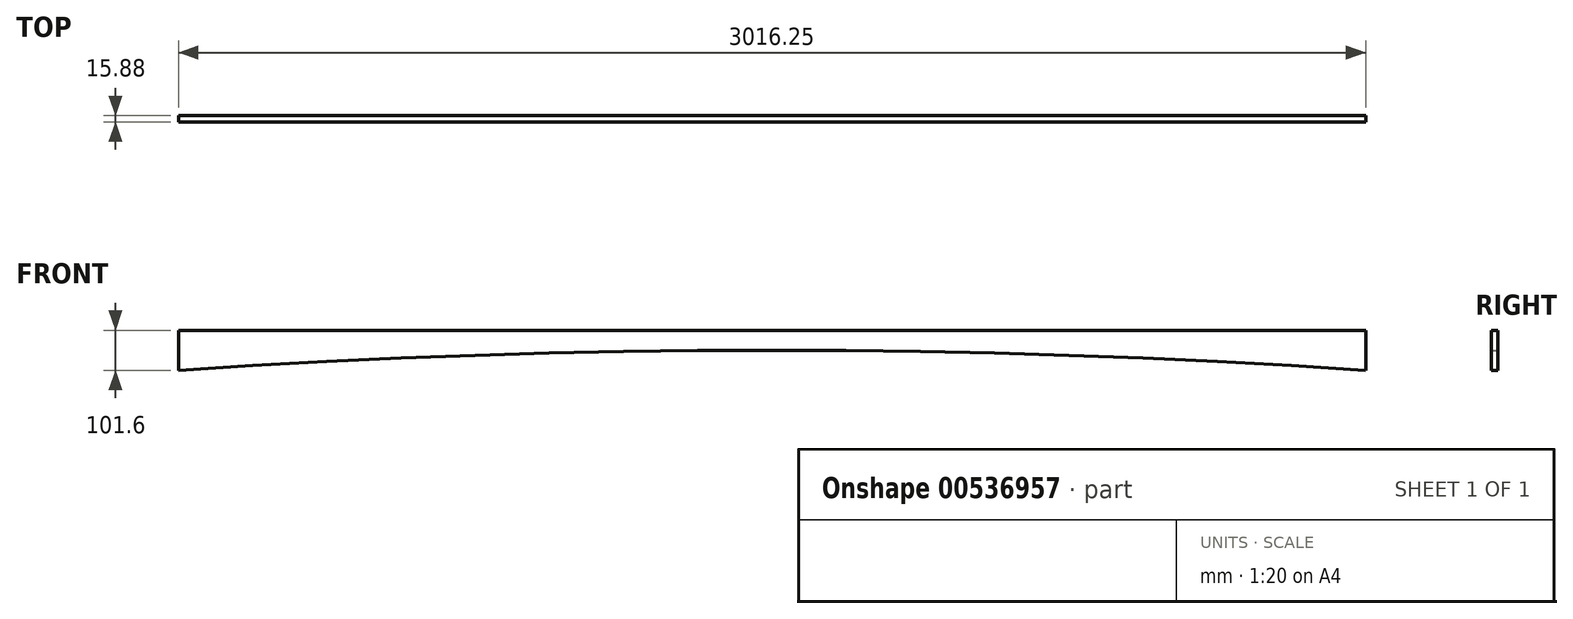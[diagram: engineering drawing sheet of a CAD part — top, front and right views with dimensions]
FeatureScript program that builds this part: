
annotation { "Feature Type Name" : "Feature", "Feature Type Description" : "" }
export const myFeature = defineFeature(function(context is Context, id is Id, definition is map)
    precondition{}
    {
        {
            var Q0;
            Q0=qCreatedBy(makeId("Front.planeOp"),FACE);
            var sketch = newSketch(context, id + "F0", { "sketchPlane" : qUnion([Q0])});
            skLineSegment(sketch, "E0", {"start": v(-115.17, 28.94) * mm, "end": v(3002.68, 28.94) * mm});
            skLineSegment(sketch, "E1", {"start": v(3002.68, 28.94) * mm, "end": v(3002.68, -47.26) * mm});
            skLineSegment(sketch, "E2", {"start": v(-115.17, 28.94) * mm, "end": v(-115.17, -47.26) * mm});
            skArc(sketch, "E3", {"start": v(3002.68, -47.26) * mm, "mid": v(1443.75, 3.54) * mm, "end": v(-115.17, -47.26) * mm});
            skPoint(sketch, "E4.start.orphan", {"position": v(1443.75, 28.94) * mm});
            skSolve(sketch);
        }
        {
            var Q0;
            Q0 = qSketchRegion(id + "F0", true);
            extrude(context, id + "F1", {"entities" : qUnion([Q0]), "depth" : 25.4 * mm, "offsetDistance" : 25.4 * mm});
        }
        {
            var Q0;
            Q0=makeQuery(id+"F1.opExtrude","SWEPT_BODY",BODY,{"disambiguationData":[OSD([sQuery(id+"F0.wireOp",EDGE,"E0"),sQuery(id+"F0.wireOp",EDGE,"E1"),sQuery(id+"F0.wireOp",EDGE,"E2"),sQuery(id+"F0.wireOp",EDGE,"E3")])]});
            deleteBodies(context, id + "F2", {"entities" : qUnion([Q0])});
        }
        {
            var Q0;
            Q0=qCreatedBy(makeId("Front.planeOp"),FACE);
            var sketch = newSketch(context, id + "F3", { "sketchPlane" : qUnion([Q0])});
            skLineSegment(sketch, "E5", {"start": v(-68.75, -37.72) * mm, "end": v(2947.5, -37.72) * mm});
            skLineSegment(sketch, "E6", {"start": v(-68.75, -37.72) * mm, "end": v(-68.75, -139.32) * mm});
            skLineSegment(sketch, "E7", {"start": v(2947.5, -37.72) * mm, "end": v(2947.5, -139.32) * mm});
            skArc(sketch, "E8", {"start": v(2947.5, -139.32) * mm, "mid": v(1439.38, -88.52) * mm, "end": v(-68.75, -139.32) * mm});
            skPoint(sketch, "E9.start.orphan", {"position": v(-68.75, 205.88) * mm});
            skPoint(sketch, "E10.start.orphan", {"position": v(1439.38, -37.72) * mm});
            skSolve(sketch);
        }
        {
            var Q0;
            Q0 = qSketchRegion(id + "F3", true);
            extrude(context, id + "F4", {"entities" : qUnion([Q0]), "depth" : 15.88 * mm, "offsetDistance" : 25.4 * mm});
        }
    });
